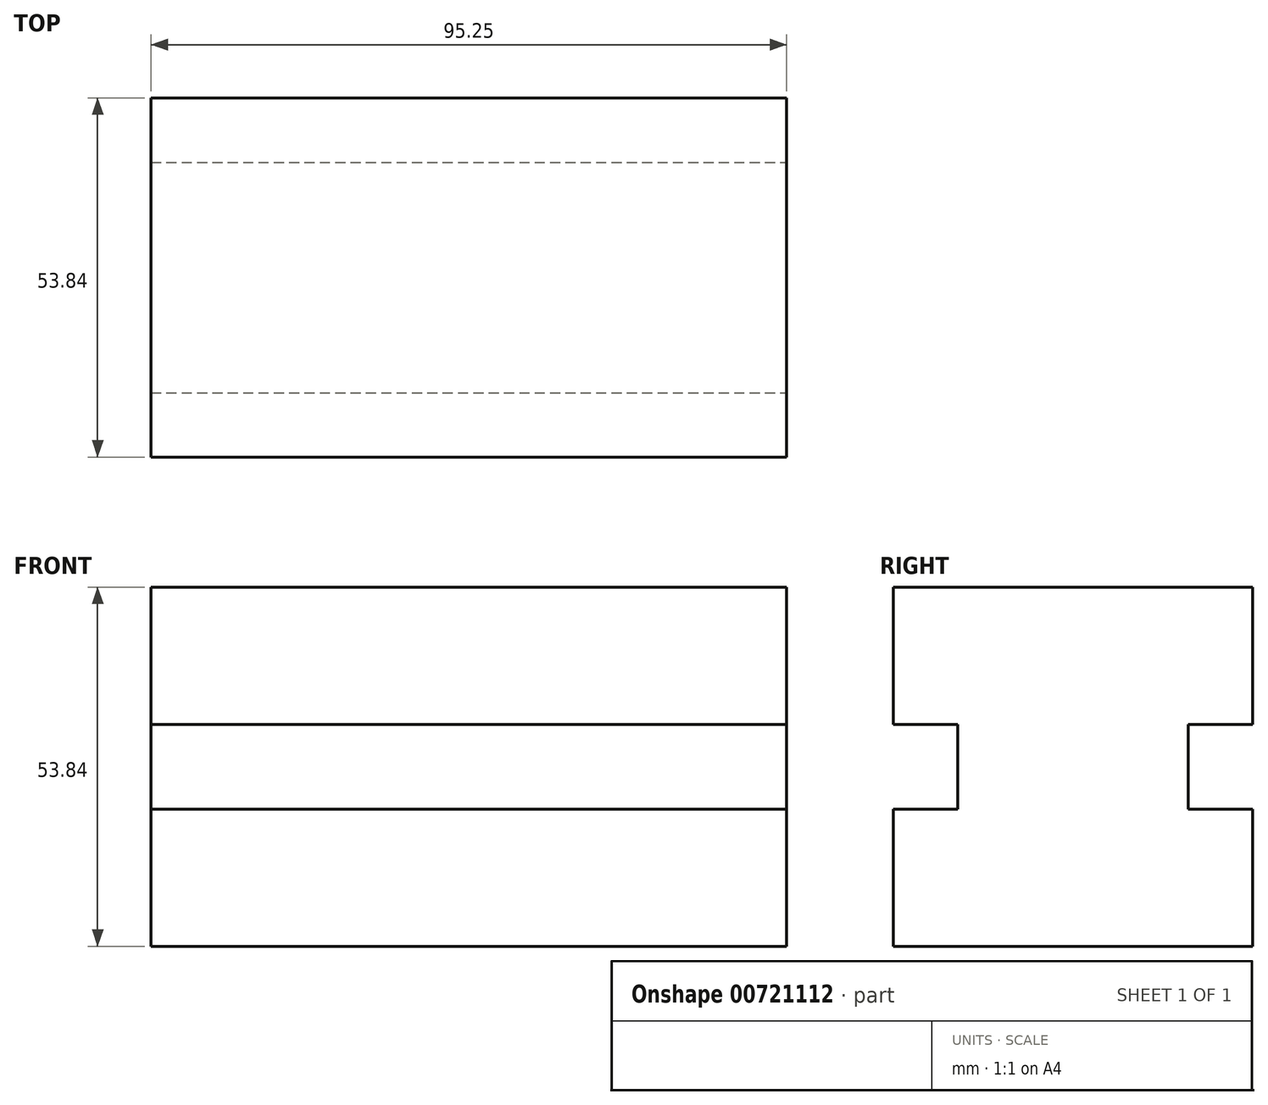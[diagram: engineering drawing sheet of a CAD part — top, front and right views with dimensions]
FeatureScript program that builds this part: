
annotation { "Feature Type Name" : "Feature", "Feature Type Description" : "" }
export const myFeature = defineFeature(function(context is Context, id is Id, definition is map)
    precondition{}
    {
        {
            var Q0;
            Q0=qCreatedBy(makeId("Right.planeOp"),FACE);
            var sketch = newSketch(context, id + "F0", { "sketchPlane" : qUnion([Q0])});
            skLineSegment(sketch, "E0.bottom", {"start": v(26.92, -26.92) * mm, "end": v(-26.92, -26.92) * mm});
            skLineSegment(sketch, "E0.top", {"start": v(26.92, 26.92) * mm, "end": v(-26.92, 26.92) * mm});
            skLineSegment(sketch, "E0.left", {"start": v(26.92, -26.92) * mm, "end": v(26.92, -6.35) * mm});
            skLineSegment(sketch, "E0.right", {"start": v(-26.92, -26.92) * mm, "end": v(-26.92, -6.35) * mm});
            skPoint(sketch, "E0.middle", {"position": v(0, 0) * mm});
            skLineSegment(sketch, "E1.bottom", {"start": v(-26.92, 6.35) * mm, "end": v(-17.27, 6.35) * mm});
            skLineSegment(sketch, "E1.top", {"start": v(-26.92, -6.35) * mm, "end": v(-17.27, -6.35) * mm});
            skLineSegment(sketch, "E1.right", {"start": v(-17.27, 6.35) * mm, "end": v(-17.27, -6.35) * mm});
            skLineSegment(sketch, "E2", {"start": v(0, 35.93) * mm, "end": v(0, -36.17) * mm, "construction": true});
            skPoint(sketch, "E2.startSnap0", {"position": v(0, 26.92) * mm});
            skLineSegment(sketch, "E3.MirrorCS", {"start": v(26.92, 6.35) * mm, "end": v(17.27, 6.35) * mm});
            skLineSegment(sketch, "E4.MirrorCS", {"start": v(17.27, 6.35) * mm, "end": v(17.27, -6.35) * mm});
            skLineSegment(sketch, "E5.MirrorCS", {"start": v(26.92, -6.35) * mm, "end": v(17.27, -6.35) * mm});
            skLineSegment(sketch, "E6.trimOffspring", {"start": v(-26.92, 6.35) * mm, "end": v(-26.92, 26.92) * mm});
            skLineSegment(sketch, "E7.trimOffspring", {"start": v(26.92, 6.35) * mm, "end": v(26.92, 26.92) * mm});
            skSolve(sketch);
        }
        {
            var Q0;
            Q0=makeQuery(id+"F0.imprint","IMPRINT",FACE,{"disambiguationData":[TD([[makeQuery(id+"F0.imprint","IMPRINT",EDGE,{"derivedFrom":sQuery(id+"F0.wireOp",EDGE,"E0.bottom")}),-1.0]])]});
            extrude(context, id + "F1", {"entities" : qUnion([Q0]), "oppositeDirection" : true, "depth" : 95.25 * mm, "offsetDistance" : 25.4 * mm});
        }
    });
